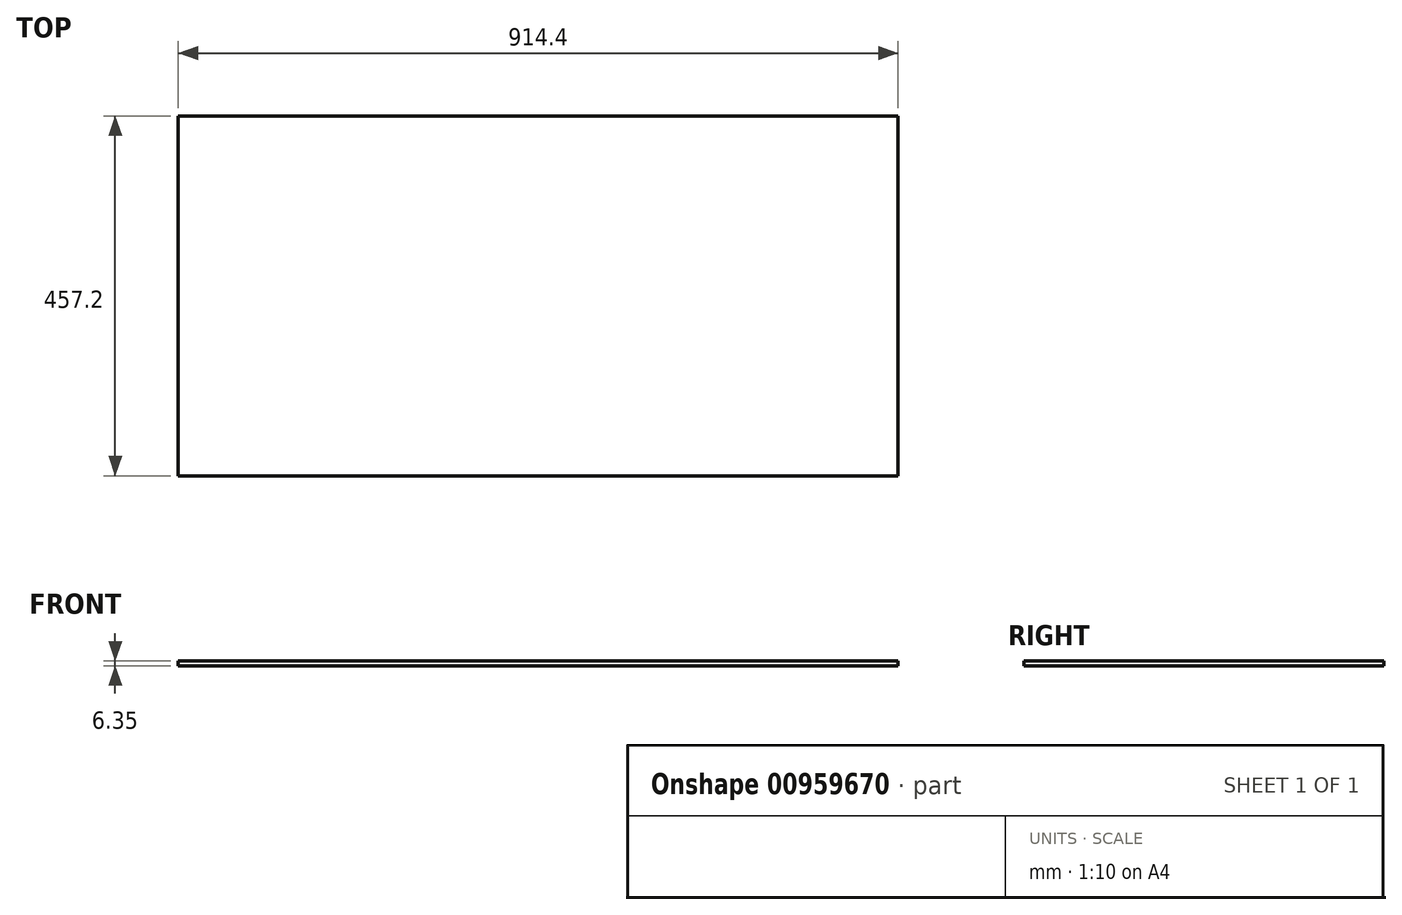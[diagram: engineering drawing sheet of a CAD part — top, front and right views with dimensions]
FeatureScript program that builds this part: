
annotation { "Feature Type Name" : "Feature", "Feature Type Description" : "" }
export const myFeature = defineFeature(function(context is Context, id is Id, definition is map)
    precondition{}
    {
        {
            var Q0;
            Q0=qCreatedBy(makeId("Top.planeOp"),FACE);
            var sketch = newSketch(context, id + "F0", { "sketchPlane" : qUnion([Q0])});
            skLineSegment(sketch, "E0.bottom", {"start": v(-477.02, 364.5) * mm, "end": v(437.38, 364.5) * mm});
            skLineSegment(sketch, "E0.top", {"start": v(-477.02, -92.7) * mm, "end": v(437.38, -92.7) * mm});
            skLineSegment(sketch, "E0.left", {"start": v(-477.02, 364.5) * mm, "end": v(-477.02, -92.7) * mm});
            skLineSegment(sketch, "E0.right", {"start": v(437.38, 364.5) * mm, "end": v(437.38, -92.7) * mm});
            skSolve(sketch);
        }
        {
            var Q0;
            Q0=makeQuery(id+"F0.imprint","IMPRINT",FACE,{"disambiguationData":[TD([[makeQuery(id+"F0.imprint","IMPRINT",EDGE,{"derivedFrom":sQuery(id+"F0.wireOp",EDGE,"E0.bottom")}),-1.0]])]});
            extrude(context, id + "F1", {"entities" : qUnion([Q0]), "depth" : 6.35 * mm, "offsetDistance" : 25.4 * mm});
        }
    });
